# Revit family: xxxBasin-Countertop-American_Standard-Cadet_Everclean-0419XXX_Series
name_source: partatom
category: Plumbing Fixtures
units: mm (PartAtom-declared; Revit-internal decimal feet)

## family parameters
Always vertical = No
Cut with Voids When Loaded = Yes
OmniClass Number = 23.45.05.14.14
OmniClass Title = Sinks/Lavatories
Part Type = Normal
Room Calculation Point = No
Round Connector Dimension = Use Diameter
Shared = Yes
Work Plane-Based = Yes

## types (2) — shared parameters
ADA Compliant = Yes
ANSI A117.1 Accessible and Usable Buildings and Facilities = Yes
ASME A112.19.2/CSA B45.1 = Yes
Assembly Code = D2010310
Basin Shape = Oval
Bowl Length = 11"
Bowl Width = 16 1/2"
CW Connection = Yes
CWFU = 2
Cold Water Connection Diameter = 3/8"
Default Elevation = 0"
Front Overflow = Yes
HW Connection = Yes
HW/CW Connection Depth = 10 3/4"
HWFU = 2
Height = 7 1/2"
Height A.F.F = 33 1/4"
Hot Water Connection Diameter = 0"
Installation Type = Countertop Sink
Length = 17 5/8"
Manufacturer = American Standard
Optional Splashback (Min. 2 3/8") = 2 3/8"
Price = Prices may vary. Please consult Manufacturer Representative for most up-to-date price list.
Product Documentation Link = https://americanstandard.box.com
Product Page URL = https://www.americanstandard.ca
Revised Date = 04/11/2022
Setback- Drain = 7 7/8"
Setback- Faucet Holes = 2 3/4"
Splashback Setback = 2 3/8"
Supplied With Cut-out Template = Yes
URL = https://www.americanstandard.ca
Vent Connection = No
WFU = 3
Waste Connection = Yes
Waste Connection Depth = 12 7/8"
Width = 21"

## per-type parameters (varying)
| type | 4" Centreset | 4" Centreset Constraint | Center Hole | Description | Finish | Material | Waste Connection Diameter |
| 0419.444EC.021 | Yes | 8 1/2" | No | Cadet Oval Countertop Sink 4-Inch Centers with EverClean | Vitreous China-American Standard-021-Bone | Vitreous China-American Standard-021-Bone | 1 1/4" |
| 0419.111EC.020 | No | 6" | Yes | Cadet Oval Countertop Sink Center Hole Only with EverClean | Vitreous China-American Standard-020-White | Vitreous China-American Standard-020-White | 1 3/4" |

note: column(s) folded — value = type name in every type: Model

## geometry (parser evidence)
native form markers: Sweep x2
no freeform markers — native parametric forms only
